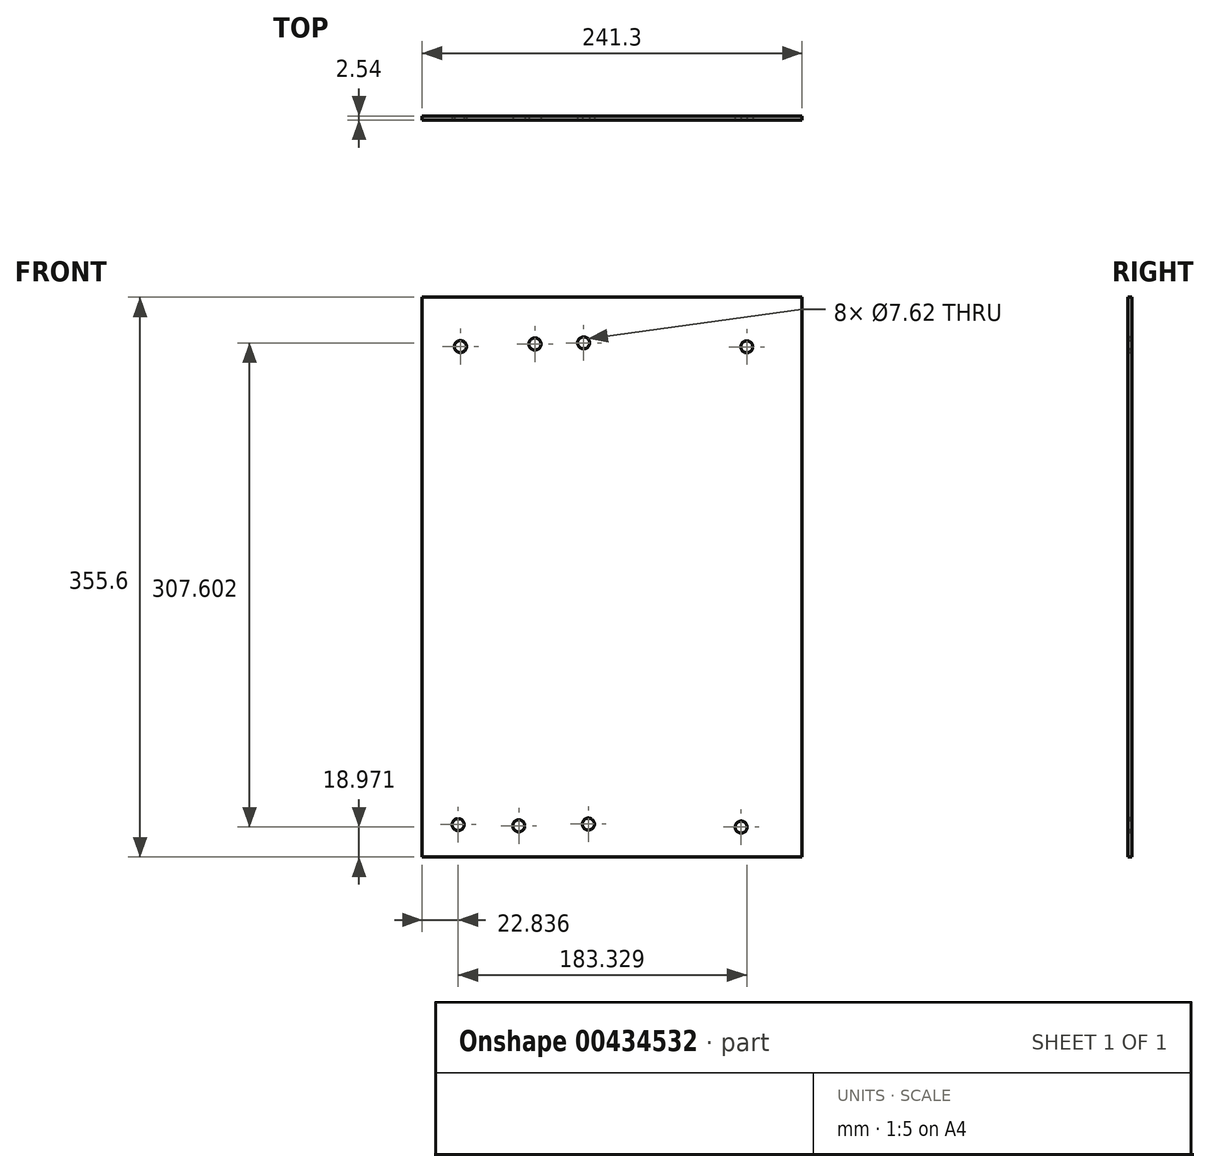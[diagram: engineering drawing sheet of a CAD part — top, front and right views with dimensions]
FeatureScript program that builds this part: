
annotation { "Feature Type Name" : "Feature", "Feature Type Description" : "" }
export const myFeature = defineFeature(function(context is Context, id is Id, definition is map)
    precondition{}
    {
        {
            var Q0;
            Q0=qCreatedBy(makeId("Front.planeOp"),FACE);
            var sketch = newSketch(context, id + "F0", { "sketchPlane" : qUnion([Q0])});
            skLineSegment(sketch, "E0.bottom", {"start": v(-120.65, 177.8) * mm, "end": v(120.65, 177.8) * mm});
            skLineSegment(sketch, "E0.top", {"start": v(-120.65, -177.8) * mm, "end": v(120.65, -177.8) * mm});
            skLineSegment(sketch, "E0.left", {"start": v(-120.65, 177.8) * mm, "end": v(-120.65, -177.8) * mm});
            skLineSegment(sketch, "E0.right", {"start": v(120.65, 177.8) * mm, "end": v(120.65, -177.8) * mm});
            skPoint(sketch, "E0.middle", {"position": v(0, 0) * mm});
            skSolve(sketch);
        }
        {
            var Q0;
            Q0 = qSketchRegion(id + "F0", true);
            extrude(context, id + "F1", {"entities" : qUnion([Q0]), "depth" : 2.54 * mm});
        }
        {
            var Q0;
            Q0=makeQuery(id+"F1.opExtrude","CAP_FACE",FACE,{"disambiguationData":[OSD([sQuery(id+"F0.wireOp",EDGE,"E0.bottom"),sQuery(id+"F0.wireOp",EDGE,"E0.top"),sQuery(id+"F0.wireOp",EDGE,"E0.left"),sQuery(id+"F0.wireOp",EDGE,"E0.right")])],"isStart":false});
            var sketch = newSketch(context, id + "F2", { "sketchPlane" : qUnion([Q0])});
            skCircle(sketch, "E1", {"center": v(-97.81, -157.27) * mm, "radius": 3.81 * mm});
            skCircle(sketch, "E2", {"center": v(-96.32, 146.4) * mm, "radius": 3.81 * mm});
            skCircle(sketch, "E3", {"center": v(-59.3, -158.03) * mm, "radius": 3.81 * mm});
            skCircle(sketch, "E4", {"center": v(-49, 148.01) * mm, "radius": 3.81 * mm});
            skCircle(sketch, "E5", {"center": v(-15.05, -156.89) * mm, "radius": 3.81 * mm});
            skCircle(sketch, "E6", {"center": v(-18.1, 148.77) * mm, "radius": 3.81 * mm});
            skSolve(sketch);
        }
        {
            var Q0;
            Q0=sQuery(id+"F2.wireOp",VERTEX,"E1.center");
            var Q1;
            Q1=sQuery(id+"F2.wireOp",VERTEX,"E3.center");
            var Q2;
            Q2=sQuery(id+"F2.wireOp",VERTEX,"E5.center");
            var Q3;
            Q3=sQuery(id+"F2.wireOp",VERTEX,"E6.center");
            var Q4;
            Q4=sQuery(id+"F2.wireOp",VERTEX,"E4.center");
            var Q5;
            Q5=sQuery(id+"F2.wireOp",VERTEX,"E2.center");
            var Q6;
            Q6=makeQuery(id+"F1.opExtrude","SWEPT_BODY",BODY,{"disambiguationData":[OSD([sQuery(id+"F0.wireOp",EDGE,"E0.bottom"),sQuery(id+"F0.wireOp",EDGE,"E0.top"),sQuery(id+"F0.wireOp",EDGE,"E0.left"),sQuery(id+"F0.wireOp",EDGE,"E0.right")])]});
            hole(context, id + "F3", {"style" : HoleStyle.SIMPLE, "endStyle" : HoleEndStyle.THROUGH, "holeDiameter" : 7.62 * mm, "isTappedThrough" : true, "tappedDepth" : 12.7 * mm, "tapClearance" : 3, "locations" : qUnion([Q0, Q1, Q2, Q3, Q4, Q5]), "scope" : qUnion([Q6])});
        }
        {
            var Q0;
            Q0=makeQuery(id+"F1.opExtrude","CAP_FACE",FACE,{"disambiguationData":[OSD([sQuery(id+"F0.wireOp",EDGE,"E0.bottom"),sQuery(id+"F0.wireOp",EDGE,"E0.top"),sQuery(id+"F0.wireOp",EDGE,"E0.left"),sQuery(id+"F0.wireOp",EDGE,"E0.right")])],"isStart":false});
            var sketch = newSketch(context, id + "F4", { "sketchPlane" : qUnion([Q0])});
            skCircle(sketch, "E7", {"center": v(81.95, -158.83) * mm, "radius": 3.8 * mm});
            skSolve(sketch);
        }
        {
            var Q0;
            Q0=sQuery(id+"F4.wireOp",VERTEX,"E7.center");
            var Q1;
            Q1=makeQuery(id+"F1.opExtrude","SWEPT_BODY",BODY,{"disambiguationData":[OSD([sQuery(id+"F0.wireOp",EDGE,"E0.bottom"),sQuery(id+"F0.wireOp",EDGE,"E0.top"),sQuery(id+"F0.wireOp",EDGE,"E0.left"),sQuery(id+"F0.wireOp",EDGE,"E0.right")])]});
            hole(context, id + "F5", {"style" : HoleStyle.SIMPLE, "endStyle" : HoleEndStyle.THROUGH, "holeDiameter" : 7.62 * mm, "isTappedThrough" : true, "tappedDepth" : 12.7 * mm, "tapClearance" : 3, "locations" : qUnion([Q0]), "scope" : qUnion([Q1])});
        }
        {
            var Q0;
            Q0=makeQuery(id+"F1.opExtrude","CAP_FACE",FACE,{"disambiguationData":[OSD([sQuery(id+"F0.wireOp",EDGE,"E0.bottom"),sQuery(id+"F0.wireOp",EDGE,"E0.top"),sQuery(id+"F0.wireOp",EDGE,"E0.left"),sQuery(id+"F0.wireOp",EDGE,"E0.right")])],"isStart":false});
            var sketch = newSketch(context, id + "F6", { "sketchPlane" : qUnion([Q0])});
            skCircle(sketch, "E8", {"center": v(85.51, 146.25) * mm, "radius": 3.81 * mm});
            skSolve(sketch);
        }
        {
            var Q0;
            Q0=sQuery(id+"F6.wireOp",VERTEX,"E8.center");
            var Q1;
            Q1=makeQuery(id+"F1.opExtrude","SWEPT_BODY",BODY,{"disambiguationData":[OSD([sQuery(id+"F0.wireOp",EDGE,"E0.bottom"),sQuery(id+"F0.wireOp",EDGE,"E0.top"),sQuery(id+"F0.wireOp",EDGE,"E0.left"),sQuery(id+"F0.wireOp",EDGE,"E0.right")])]});
            hole(context, id + "F7", {"style" : HoleStyle.SIMPLE, "endStyle" : HoleEndStyle.THROUGH, "holeDiameter" : 7.62 * mm, "isTappedThrough" : true, "tappedDepth" : 12.7 * mm, "tapClearance" : 3, "locations" : qUnion([Q0]), "scope" : qUnion([Q1])});
        }
    });
